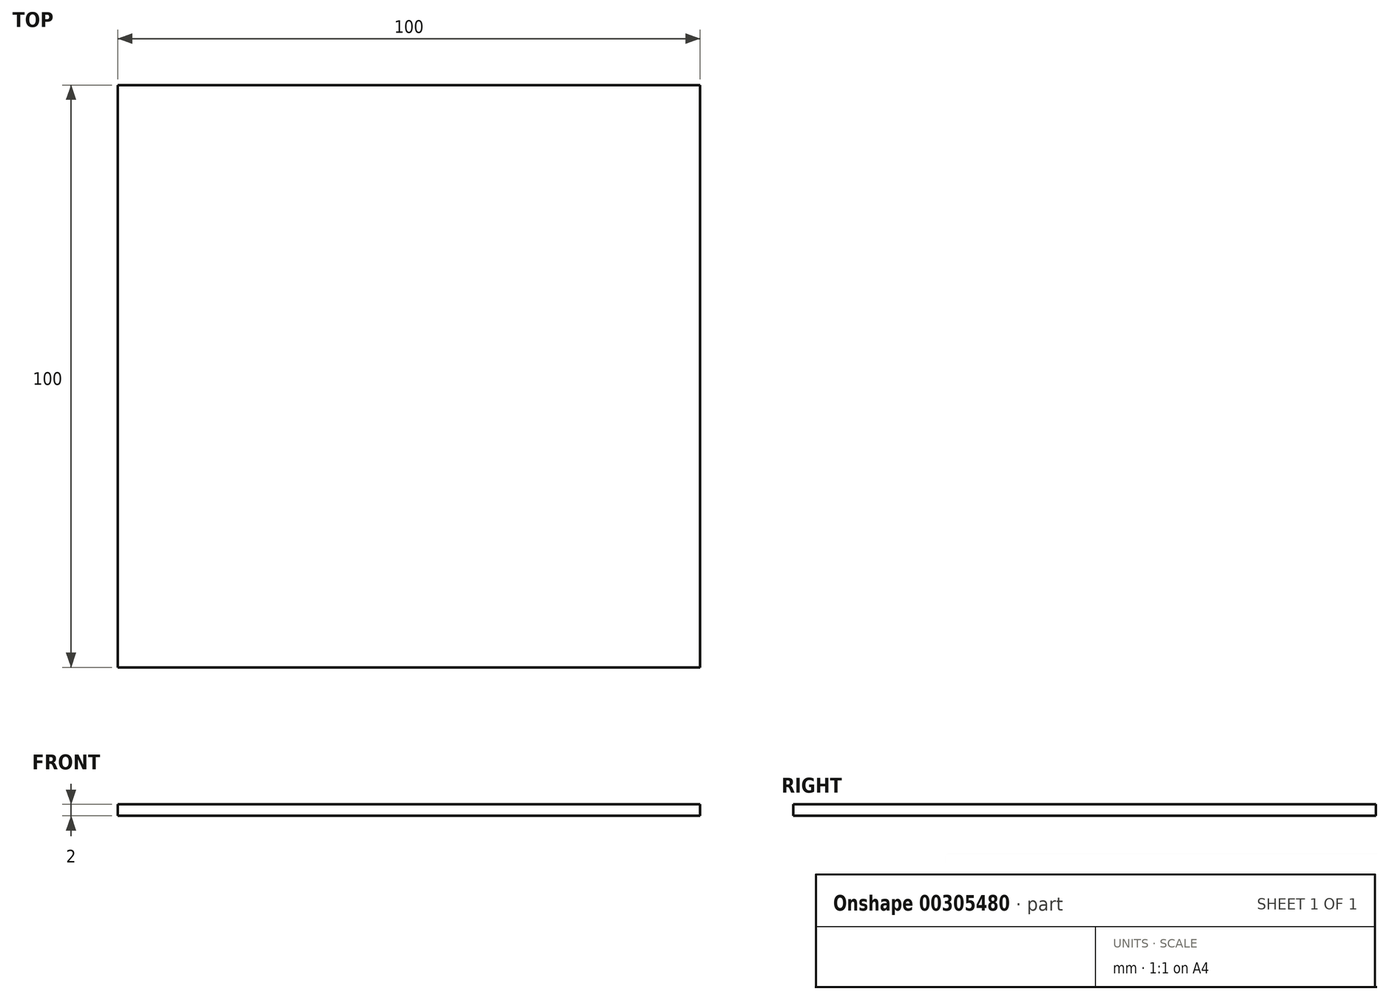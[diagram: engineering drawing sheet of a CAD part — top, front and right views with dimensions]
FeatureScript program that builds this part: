
annotation { "Feature Type Name" : "Feature", "Feature Type Description" : "" }
export const myFeature = defineFeature(function(context is Context, id is Id, definition is map)
    precondition{}
    {
        {
            var Q0;
            Q0=qCreatedBy(makeId("Top.planeOp"),FACE);
            var sketch = newSketch(context, id + "F0", { "sketchPlane" : qUnion([Q0])});
            skLineSegment(sketch, "E0", {"start": v(-50, -50) * mm, "end": v(50, -50) * mm});
            skLineSegment(sketch, "E1", {"start": v(50, -50) * mm, "end": v(50, 50) * mm});
            skLineSegment(sketch, "E2", {"start": v(-50, -50) * mm, "end": v(-50, 50) * mm});
            skLineSegment(sketch, "E3", {"start": v(50, 50) * mm, "end": v(-50, 50) * mm});
            skSolve(sketch);
        }
        {
            var Q0;
            Q0 = qSketchRegion(id + "F0", true);
            extrude(context, id + "F1", {"entities" : qUnion([Q0]), "depth" : 2 * mm});
        }
    });
